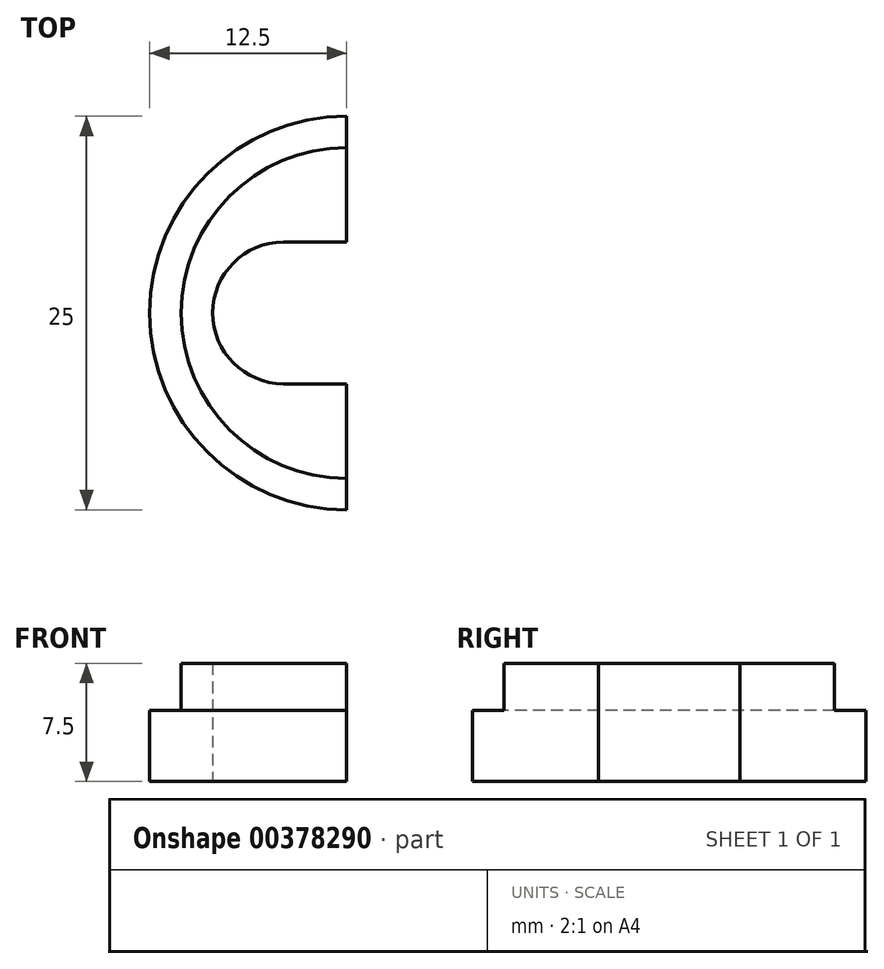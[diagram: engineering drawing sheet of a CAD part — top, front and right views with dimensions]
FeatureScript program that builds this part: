
annotation { "Feature Type Name" : "Feature", "Feature Type Description" : "" }
export const myFeature = defineFeature(function(context is Context, id is Id, definition is map)
    precondition{}
    {
        {
            var Q0;
            Q0=qCreatedBy(makeId("Top.planeOp"),FACE);
            var sketch = newSketch(context, id + "F0", { "sketchPlane" : qUnion([Q0])});
            skCircle(sketch, "E0", {"center": v(0, 0) * mm, "radius": 10.5 * mm});
            skCircle(sketch, "E1", {"center": v(0, 0) * mm, "radius": 12.5 * mm});
            skLineSegment(sketch, "E2", {"start": v(0, 12.5) * mm, "end": v(0, 10.5) * mm});
            skLineSegment(sketch, "E3", {"start": v(0, 10.5) * mm, "end": v(0, -10.5) * mm});
            skLineSegment(sketch, "E4", {"start": v(0, -10.5) * mm, "end": v(0, -12.5) * mm});
            skCircle(sketch, "E5", {"center": v(-4, 0) * mm, "radius": 4.5 * mm});
            skLineSegment(sketch, "E6", {"start": v(-4, 4.5) * mm, "end": v(0, 4.5) * mm});
            skLineSegment(sketch, "E7", {"start": v(0, 4.5) * mm, "end": v(0, -4.5) * mm});
            skLineSegment(sketch, "E8", {"start": v(0, -4.5) * mm, "end": v(-4, -4.5) * mm});
            skSolve(sketch);
        }
        {
            var Q0;
            {var subQ0=sQuery(id+"F0.wireOp",EDGE,"E6");Q0=makeQuery(id+"F0.imprint","IMPRINT",FACE,{"disambiguationData":[TD([[makeQuery(id+"F0.imprint","IMPRINT",EDGE,{"derivedFrom":subQ0}),1.0]])]});}
            extrude(context, id + "F1", {"entities" : qUnion([Q0]), "depth" : 7.5 * mm});
        }
        {
            var Q0;
            {var subQ1=sQuery(id+"F0.wireOp",EDGE,"E2");Q0=makeQuery(id+"F0.imprint","IMPRINT",FACE,{"disambiguationData":[TD([[makeQuery(id+"F0.imprint","IMPRINT",EDGE,{"derivedFrom":subQ1}),-1.0]])]});}
            extrude(context, id + "F2", {"entities" : qUnion([Q0]), "operationType" : NewBodyOperationType.ADD, "depth" : 4.5 * mm});
        }
    });
